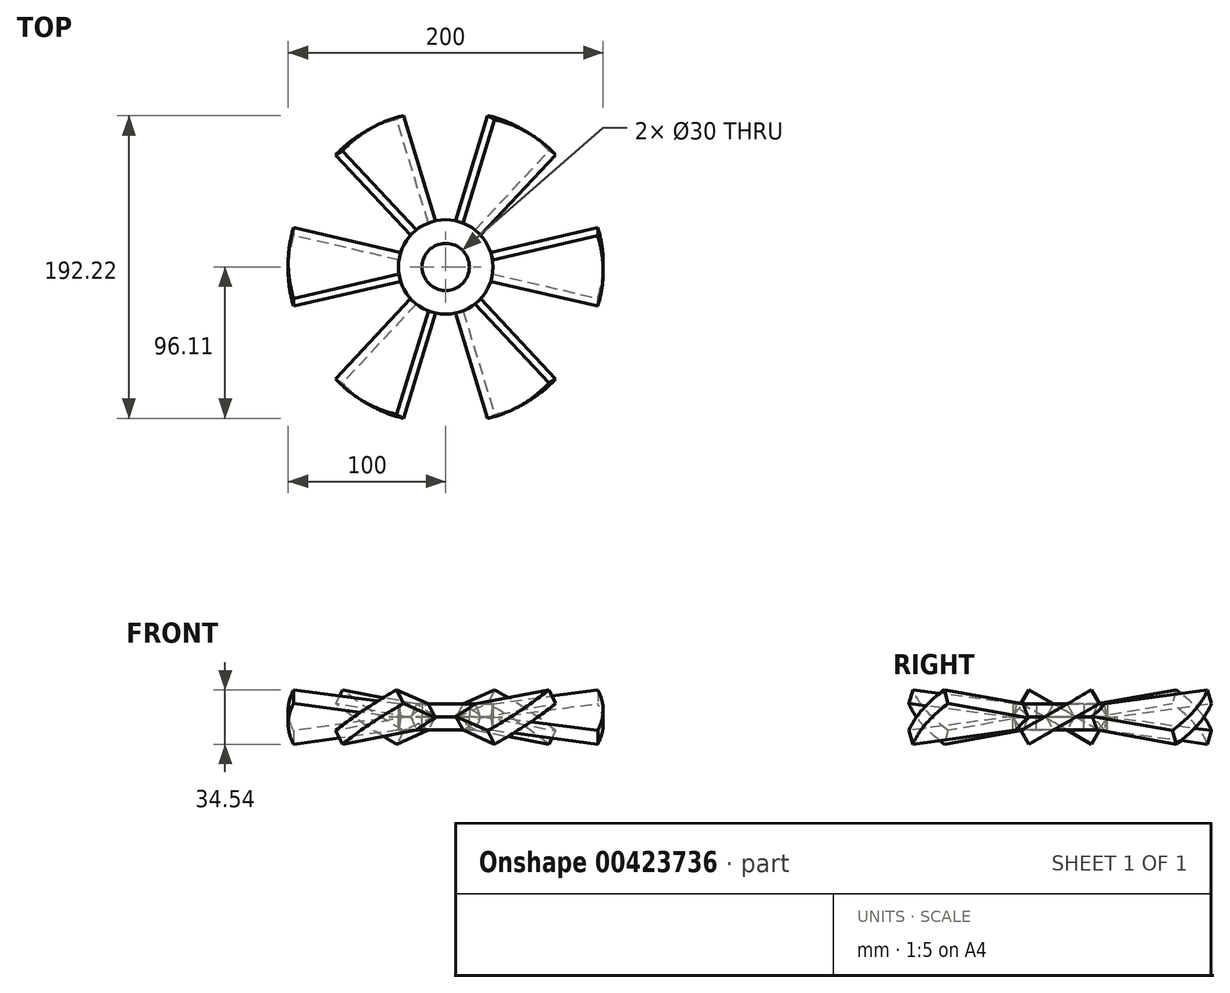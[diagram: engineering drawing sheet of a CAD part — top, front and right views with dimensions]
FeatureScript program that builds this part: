
annotation { "Feature Type Name" : "Feature", "Feature Type Description" : "" }
export const myFeature = defineFeature(function(context is Context, id is Id, definition is map)
    precondition{}
    {
        {
            var Q0;
            Q0=qCreatedBy(makeId("Top.planeOp"),FACE);
            var sketch = newSketch(context, id + "F0", { "sketchPlane" : qUnion([Q0])});
            skCircle(sketch, "E0", {"center": v(0, 0) * mm, "radius": 100 * mm});
            skLineSegment(sketch, "E1", {"start": v(0, 0) * mm, "end": v(96.6, -25.88) * mm});
            skLineSegment(sketch, "E2", {"start": v(0, 0) * mm, "end": v(96.6, 25.88) * mm});
            skLineSegment(sketch, "E3", {"start": v(0, 0) * mm, "end": v(-177.99, 0) * mm});
            skSolve(sketch);
        }
        {
            var Q0;
            {var subQ0=sQuery(id+"F0.wireOp",EDGE,"E1");Q0=makeQuery(id+"F0.imprint","IMPRINT",FACE,{"disambiguationData":[TD([[makeQuery(id+"F0.imprint","IMPRINT",EDGE,{"derivedFrom":subQ0}),1.0]])]});}
            extrude(context, id + "F1", {"entities" : qUnion([Q0]), "endBound" : BoundingType.SYMMETRIC, "depth" : 10 * mm});
        }
        {
            var Q0;
            Q0=makeQuery(id+"F1.opExtrude","SWEPT_BODY",BODY,{"disambiguationData":[OSD([sQuery(id+"F0.wireOp",EDGE,"E0"),sQuery(id+"F0.wireOp",EDGE,"E1"),sQuery(id+"F0.wireOp",EDGE,"E2")])]});
            var Q1;
            Q1=sQuery(id+"F0.wireOp",EDGE,"E3");
            transform(context, id + "F2", {"entities" : qUnion([Q0]), "transformType" : TransformType.ROTATION, "transformAxis" : qUnion([Q1]), "angle" : 30 * degree, "oppositeDirection" : true, "makeCopy" : false});
        }
        {
            var Q0;
            Q0=qCreatedBy(makeId("Front.planeOp"),FACE);
            var sketch = newSketch(context, id + "F3", { "sketchPlane" : qUnion([Q0])});
            skLineSegment(sketch, "E4", {"start": v(0, 0) * mm, "end": v(0, 101.99) * mm});
            skSolve(sketch);
        }
        {
            var Q0;
            Q0=makeQuery(id+"F1.opExtrude","SWEPT_BODY",BODY,{"disambiguationData":[OSD([sQuery(id+"F0.wireOp",EDGE,"E0"),sQuery(id+"F0.wireOp",EDGE,"E1"),sQuery(id+"F0.wireOp",EDGE,"E2")])]});
            var Q1;
            Q1=sQuery(id+"F3.wireOp",EDGE,"E4");
            circularPattern(context, id + "F4", {"entities" : qUnion([Q0]), "axis" : qUnion([Q1]), "angle" : 360 * degree, "instanceCount" : 6, "equalSpace" : true});
        }
        {
            var Q0;
            Q0=qCreatedBy(makeId("Top.planeOp"),FACE);
            var sketch = newSketch(context, id + "F5", { "sketchPlane" : qUnion([Q0])});
            skCircle(sketch, "E5", {"center": v(0, 0) * mm, "radius": 30 * mm});
            skSolve(sketch);
        }
        {
            var Q0;
            Q0 = qSketchRegion(id + "F5", true);
            extrude(context, id + "F6", {"entities" : qUnion([Q0]), "operationType" : NewBodyOperationType.REMOVE, "endBound" : BoundingType.SYMMETRIC, "oppositeDirection" : true, "depth" : 25 * mm});
        }
        {
            var Q0;
            Q0=qCreatedBy(makeId("Top.planeOp"),FACE);
            var sketch = newSketch(context, id + "F7", { "sketchPlane" : qUnion([Q0])});
            skCircle(sketch, "E6", {"center": v(0, 0) * mm, "radius": 30 * mm});
            skCircle(sketch, "E7", {"center": v(0, 0) * mm, "radius": 15 * mm});
            skSolve(sketch);
        }
        {
            var Q0;
            {var subQ0=sQuery(id+"F0.wireOp",EDGE,"E2");Q0=makeQuery(id+"F6.boolean.opBoolean","INTERSECT",VERTEX,{"derivedFrom":[makeQuery(id+"F4.opPattern","COPY",FACE,{"derivedFrom":makeQuery(id+"F1.opExtrude","CAP_FACE",FACE,{"disambiguationData":[OSD([sQuery(id+"F0.wireOp",EDGE,"E0"),sQuery(id+"F0.wireOp",EDGE,"E1"),subQ0])],"isStart":false}),"instanceName":"3"}),makeQuery(id+"F4.opPattern","COPY",FACE,{"derivedFrom":makeQuery(id+"F1.opExtrude","SWEPT_FACE",FACE,{"disambiguationData":[OSD([subQ0])]}),"instanceName":"3"}),makeQuery(id+"F6.opExtrude","SWEPT_FACE",FACE,{"disambiguationData":[OSD([sQuery(id+"F5.wireOp",EDGE,"E5")])]})]});}
            var Q1;
            {var subQ0=sQuery(id+"F0.wireOp",EDGE,"E2");Q1=makeQuery(id+"F6.boolean.opBoolean","INTERSECT",VERTEX,{"derivedFrom":[makeQuery(id+"F4.opPattern","COPY",FACE,{"derivedFrom":makeQuery(id+"F1.opExtrude","CAP_FACE",FACE,{"disambiguationData":[OSD([sQuery(id+"F0.wireOp",EDGE,"E0"),sQuery(id+"F0.wireOp",EDGE,"E1"),subQ0])],"isStart":false}),"instanceName":"4"}),makeQuery(id+"F4.opPattern","COPY",FACE,{"derivedFrom":makeQuery(id+"F1.opExtrude","SWEPT_FACE",FACE,{"disambiguationData":[OSD([subQ0])]}),"instanceName":"4"}),makeQuery(id+"F6.opExtrude","SWEPT_FACE",FACE,{"disambiguationData":[OSD([sQuery(id+"F5.wireOp",EDGE,"E5")])]})]});}
            var Q2;
            {var subQ0=sQuery(id+"F0.wireOp",EDGE,"E2");Q2=makeQuery(id+"F6.boolean.opBoolean","INTERSECT",VERTEX,{"derivedFrom":[makeQuery(id+"F4.opPattern","COPY",FACE,{"derivedFrom":makeQuery(id+"F1.opExtrude","CAP_FACE",FACE,{"disambiguationData":[OSD([sQuery(id+"F0.wireOp",EDGE,"E0"),sQuery(id+"F0.wireOp",EDGE,"E1"),subQ0])],"isStart":false}),"instanceName":"5"}),makeQuery(id+"F4.opPattern","COPY",FACE,{"derivedFrom":makeQuery(id+"F1.opExtrude","SWEPT_FACE",FACE,{"disambiguationData":[OSD([subQ0])]}),"instanceName":"5"}),makeQuery(id+"F6.opExtrude","SWEPT_FACE",FACE,{"disambiguationData":[OSD([sQuery(id+"F5.wireOp",EDGE,"E5")])]})]});}
            cPlane(context, id + "F8", {"entities" : qUnion([Q0, Q1, Q2]), "cplaneType" : CPlaneType.THREE_POINT, "offset" : 25 * mm, "width" : 150 * mm, "height" : 150 * mm});
        }
        {
            var Q0;
            Q0=makeQuery(id+"F7.imprint","IMPRINT",FACE,{"disambiguationData":[TD([[makeQuery(id+"F7.imprint","IMPRINT",EDGE,{"derivedFrom":sQuery(id+"F7.wireOp",EDGE,"E6")}),1.0]])]});
            var Q1;
            Q1=qCreatedBy(id+"F8.planeOp",FACE);
            extrude(context, id + "F9", {"entities" : qUnion([Q0]), "endBound" : BoundingType.UP_TO_SURFACE, "endBoundEntityFace" : qUnion([Q1]), "depth" : 25 * mm});
        }
        {
            var Q0;
            Q0=makeQuery(id+"F9.opExtrude","SWEPT_BODY",BODY,{"disambiguationData":[OSD([sQuery(id+"F7.wireOp",EDGE,"E6"),sQuery(id+"F7.wireOp",EDGE,"E7")])]});
            var Q1;
            Q1=qCreatedBy(makeId("Top.planeOp"),FACE);
            mirror(context, id + "F10", {"entities" : qUnion([Q0]), "mirrorPlane" : qUnion([Q1])});
        }
    });
